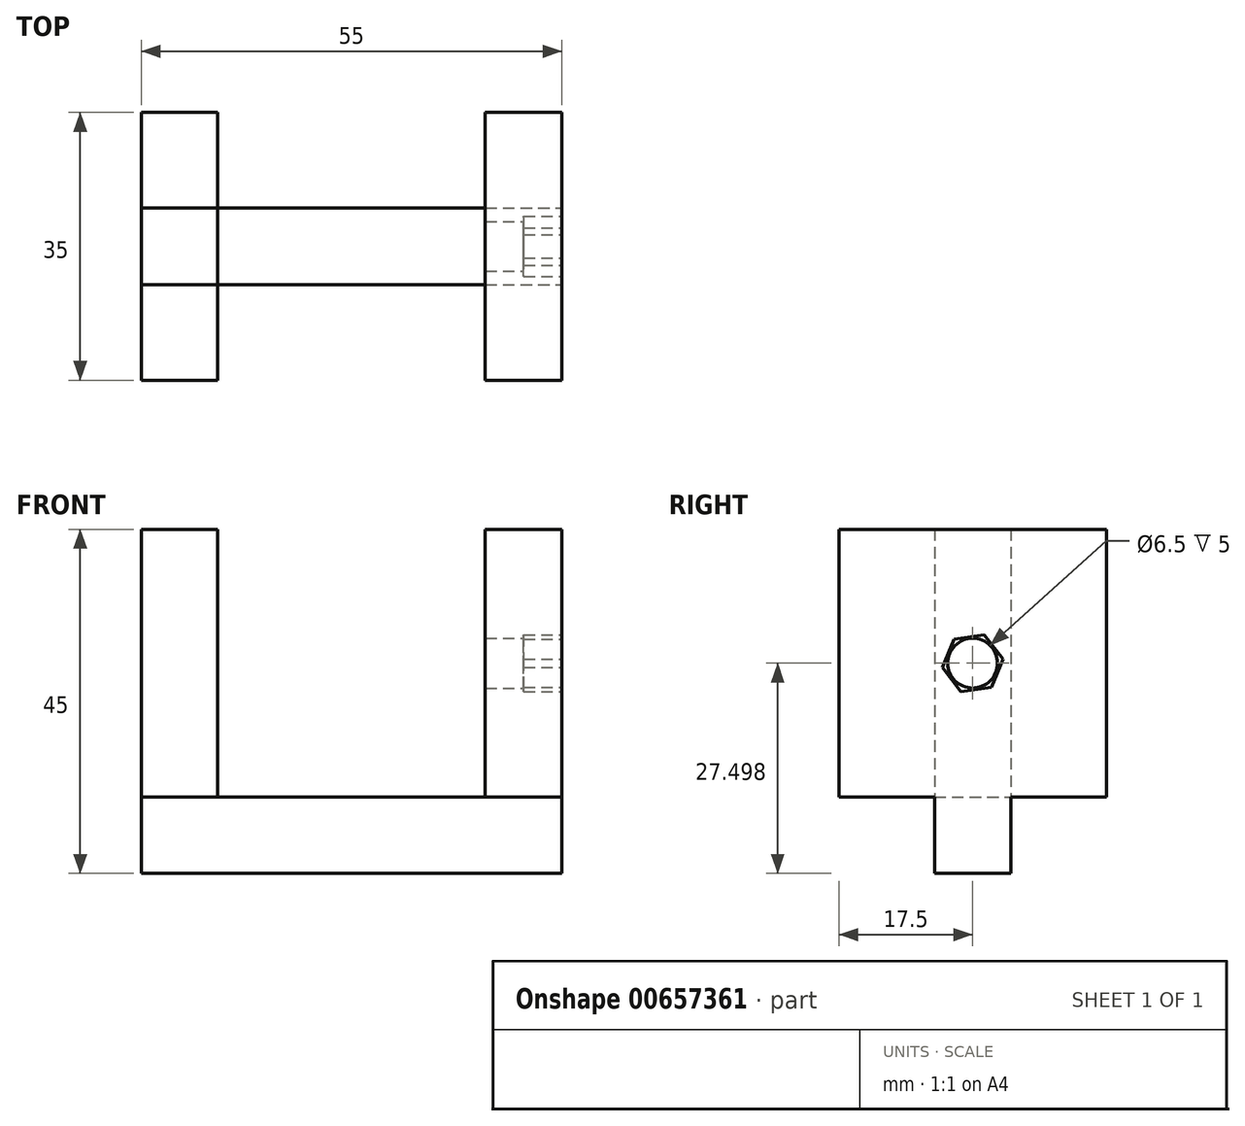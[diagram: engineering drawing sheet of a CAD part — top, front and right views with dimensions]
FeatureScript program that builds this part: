
annotation { "Feature Type Name" : "Feature", "Feature Type Description" : "" }
export const myFeature = defineFeature(function(context is Context, id is Id, definition is map)
    precondition{}
    {
        {
            var Q0;
            Q0=qCreatedBy(makeId("Front.planeOp"),FACE);
            var sketch = newSketch(context, id + "F0", { "sketchPlane" : qUnion([Q0])});
            skLineSegment(sketch, "E0", {"start": v(-22.78, 38.83) * mm, "end": v(-22.78, -6.17) * mm});
            skLineSegment(sketch, "E1", {"start": v(-22.78, -6.17) * mm, "end": v(32.22, -6.17) * mm});
            skLineSegment(sketch, "E2", {"start": v(32.22, -6.17) * mm, "end": v(32.22, 38.83) * mm});
            skLineSegment(sketch, "E3", {"start": v(32.22, 38.83) * mm, "end": v(22.22, 38.83) * mm});
            skLineSegment(sketch, "E4", {"start": v(22.22, 38.83) * mm, "end": v(22.22, 3.83) * mm});
            skLineSegment(sketch, "E5", {"start": v(22.22, 3.83) * mm, "end": v(-12.78, 3.83) * mm});
            skLineSegment(sketch, "E6", {"start": v(-12.78, 3.83) * mm, "end": v(-12.78, 38.83) * mm});
            skLineSegment(sketch, "E7", {"start": v(-12.78, 38.83) * mm, "end": v(-22.78, 38.83) * mm});
            skSolve(sketch);
        }
        {
            var Q0;
            Q0=makeQuery(id+"F0.imprint","IMPRINT",FACE,{"disambiguationData":[TD([[makeQuery(id+"F0.imprint","IMPRINT",EDGE,{"derivedFrom":sQuery(id+"F0.wireOp",EDGE,"E0")}),1.0]])]});
            extrude(context, id + "F1", {"entities" : qUnion([Q0]), "depth" : 10 * mm, "offsetDistance" : 25 * mm});
        }
        {
            var Q0;
            Q0=makeQuery(id+"F1.opExtrude","SWEPT_FACE",FACE,{"disambiguationData":[OSD([sQuery(id+"F0.wireOp",EDGE,"E2")])]});
            var sketch = newSketch(context, id + "F2", { "sketchPlane" : qUnion([Q0])});
            skLineSegment(sketch, "E8.bottom", {"start": v(-22.5, 38.83) * mm, "end": v(12.5, 38.83) * mm});
            skLineSegment(sketch, "E8.top", {"start": v(-22.5, 3.83) * mm, "end": v(12.5, 3.83) * mm});
            skLineSegment(sketch, "E8.left", {"start": v(-22.5, 38.83) * mm, "end": v(-22.5, 3.83) * mm});
            skLineSegment(sketch, "E8.right", {"start": v(12.5, 38.83) * mm, "end": v(12.5, 3.83) * mm});
            skSolve(sketch);
        }
        {
            var Q0;
            {var subQ3=sQuery(id+"F2.wireOp",EDGE,"E8.left");Q0=makeQuery(id+"F2.imprint","IMPRINT",FACE,{"disambiguationData":[TD([[makeQuery(id+"F2.imprint","IMPRINT",EDGE,{"derivedFrom":subQ3}),1.0]])]});}
            var Q1;
            {var subQ3=sQuery(id+"F2.wireOp",EDGE,"E8.right");Q1=makeQuery(id+"F2.imprint","IMPRINT",FACE,{"disambiguationData":[TD([[makeQuery(id+"F2.imprint","IMPRINT",EDGE,{"derivedFrom":subQ3}),-1.0]])]});}
            extrude(context, id + "F3", {"entities" : qUnion([Q0, Q1]), "operationType" : NewBodyOperationType.ADD, "oppositeDirection" : true, "depth" : 10 * mm, "offsetDistance" : 25 * mm});
        }
        {
            var Q0;
            Q0=makeQuery(id+"F1.opExtrude","SWEPT_FACE",FACE,{"disambiguationData":[OSD([sQuery(id+"F0.wireOp",EDGE,"E0")])]});
            var sketch = newSketch(context, id + "F4", { "sketchPlane" : qUnion([Q0])});
            skLineSegment(sketch, "E9.bottom", {"start": v(-12.5, 38.83) * mm, "end": v(22.5, 38.83) * mm});
            skLineSegment(sketch, "E9.top", {"start": v(-12.5, 3.83) * mm, "end": v(22.5, 3.83) * mm});
            skLineSegment(sketch, "E9.left", {"start": v(-12.5, 38.83) * mm, "end": v(-12.5, 3.83) * mm});
            skLineSegment(sketch, "E9.right", {"start": v(22.5, 38.83) * mm, "end": v(22.5, 3.83) * mm});
            skSolve(sketch);
        }
        {
            var Q0;
            {var subQ3=sQuery(id+"F4.wireOp",EDGE,"E9.left");Q0=makeQuery(id+"F4.imprint","IMPRINT",FACE,{"disambiguationData":[TD([[makeQuery(id+"F4.imprint","IMPRINT",EDGE,{"derivedFrom":subQ3}),1.0]])]});}
            var Q1;
            {var subQ3=sQuery(id+"F4.wireOp",EDGE,"E9.right");Q1=makeQuery(id+"F4.imprint","IMPRINT",FACE,{"disambiguationData":[TD([[makeQuery(id+"F4.imprint","IMPRINT",EDGE,{"derivedFrom":subQ3}),-1.0]])]});}
            extrude(context, id + "F5", {"entities" : qUnion([Q0, Q1]), "oppositeDirection" : true, "depth" : 10 * mm, "offsetDistance" : 25 * mm});
        }
        {
            var Q0;
            {var subQ0=sQuery(id+"F2.wireOp",EDGE,"E8.top");var subQ1=sQuery(id+"F2.wireOp",EDGE,"E8.bottom");var subQ2=sQuery(id+"F0.wireOp",EDGE,"E2");Q0=makeQuery(id+"F3.boolean.opBoolean","MERGE",FACE,{"derivedFrom":[makeQuery(id+"F1.opExtrude","SWEPT_FACE",FACE,{"disambiguationData":[OSD([subQ2])]}),makeQuery(id+"F3.opExtrude","CAP_FACE",FACE,{"disambiguationData":[OSD([subQ2,subQ1,subQ0,sQuery(id+"F2.wireOp",EDGE,"E8.left")])],"isStart":true}),makeQuery(id+"F3.opExtrude","CAP_FACE",FACE,{"disambiguationData":[OSD([subQ2,subQ1,subQ0,sQuery(id+"F2.wireOp",EDGE,"E8.right")])],"isStart":true})]});}
            var sketch = newSketch(context, id + "F6", { "sketchPlane" : qUnion([Q0])});
            skCircle(sketch, "E10", {"center": v(-5, 21.33) * mm, "radius": 3.25 * mm});
            skPoint(sketch, "E10.centerSnap0", {"position": v(-22.5, 21.33) * mm});
            skSolve(sketch);
        }
        {
            var Q0;
            Q0=makeQuery(id+"F6.imprint","IMPRINT",FACE,{"disambiguationData":[TD([[makeQuery(id+"F6.imprint","IMPRINT",EDGE,{"derivedFrom":sQuery(id+"F6.wireOp",EDGE,"E10")}),1.0]])]});
            extrude(context, id + "F7", {"entities" : qUnion([Q0]), "operationType" : NewBodyOperationType.REMOVE, "oppositeDirection" : true, "depth" : 10 * mm, "offsetDistance" : 25 * mm});
        }
        {
            var Q0;
            {var subQ0=sQuery(id+"F2.wireOp",EDGE,"E8.top");var subQ1=sQuery(id+"F2.wireOp",EDGE,"E8.bottom");var subQ2=sQuery(id+"F0.wireOp",EDGE,"E2");Q0=makeQuery(id+"F3.boolean.opBoolean","MERGE",FACE,{"derivedFrom":[makeQuery(id+"F1.opExtrude","SWEPT_FACE",FACE,{"disambiguationData":[OSD([subQ2])]}),makeQuery(id+"F3.opExtrude","CAP_FACE",FACE,{"disambiguationData":[OSD([subQ2,subQ1,subQ0,sQuery(id+"F2.wireOp",EDGE,"E8.left")])],"isStart":true}),makeQuery(id+"F3.opExtrude","CAP_FACE",FACE,{"disambiguationData":[OSD([subQ2,subQ1,subQ0,sQuery(id+"F2.wireOp",EDGE,"E8.right")])],"isStart":true})]});}
            var sketch = newSketch(context, id + "F8", { "sketchPlane" : qUnion([Q0])});
            skSolve(sketch);
        }
        {
            var Q0;
            {var subQ0=sQuery(id+"F2.wireOp",EDGE,"E8.left");Q0=makeQuery(id+"F8.imprint","IMPRINT",FACE,{"disambiguationData":[TD([[makeQuery(id+"F8.imprint","IMPRINT",EDGE,{"derivedFrom":makeQuery(id+"F3.opExtrude","CAP_EDGE",EDGE,{"disambiguationData":[OSD([subQ0])],"isStart":true})}),1.0]])]});}
            var sketch = newSketch(context, id + "F9", { "sketchPlane" : qUnion([Q0])});
            skCircle(sketch, "E11.cCircle", {"center": v(-5, 21.33) * mm, "radius": 4 * mm, "construction": true});
            skLineSegment(sketch, "E11.0", {"start": v(-3.48, 25.03) * mm, "end": v(-1.04, 21.86) * mm});
            skLineSegment(sketch, "E11.1", {"start": v(-1.04, 21.86) * mm, "end": v(-2.55, 18.16) * mm});
            skLineSegment(sketch, "E11.2", {"start": v(-2.55, 18.16) * mm, "end": v(-6.52, 17.63) * mm});
            skLineSegment(sketch, "E11.3", {"start": v(-6.52, 17.63) * mm, "end": v(-8.96, 20.8) * mm});
            skLineSegment(sketch, "E11.4", {"start": v(-8.96, 20.8) * mm, "end": v(-7.45, 24.5) * mm});
            skLineSegment(sketch, "E11.5", {"start": v(-7.45, 24.5) * mm, "end": v(-3.48, 25.03) * mm});
            skSolve(sketch);
        }
        {
            var Q0;
            Q0=makeQuery(id+"F9.imprint","IMPRINT",FACE,{"disambiguationData":[TD([[makeQuery(id+"F9.imprint","IMPRINT",EDGE,{"derivedFrom":sQuery(id+"F9.wireOp",EDGE,"E11.0")}),-1.0]])]});
            extrude(context, id + "F10", {"entities" : qUnion([Q0]), "operationType" : NewBodyOperationType.REMOVE, "oppositeDirection" : true, "depth" : 5 * mm, "offsetDistance" : 25 * mm});
        }
    });
